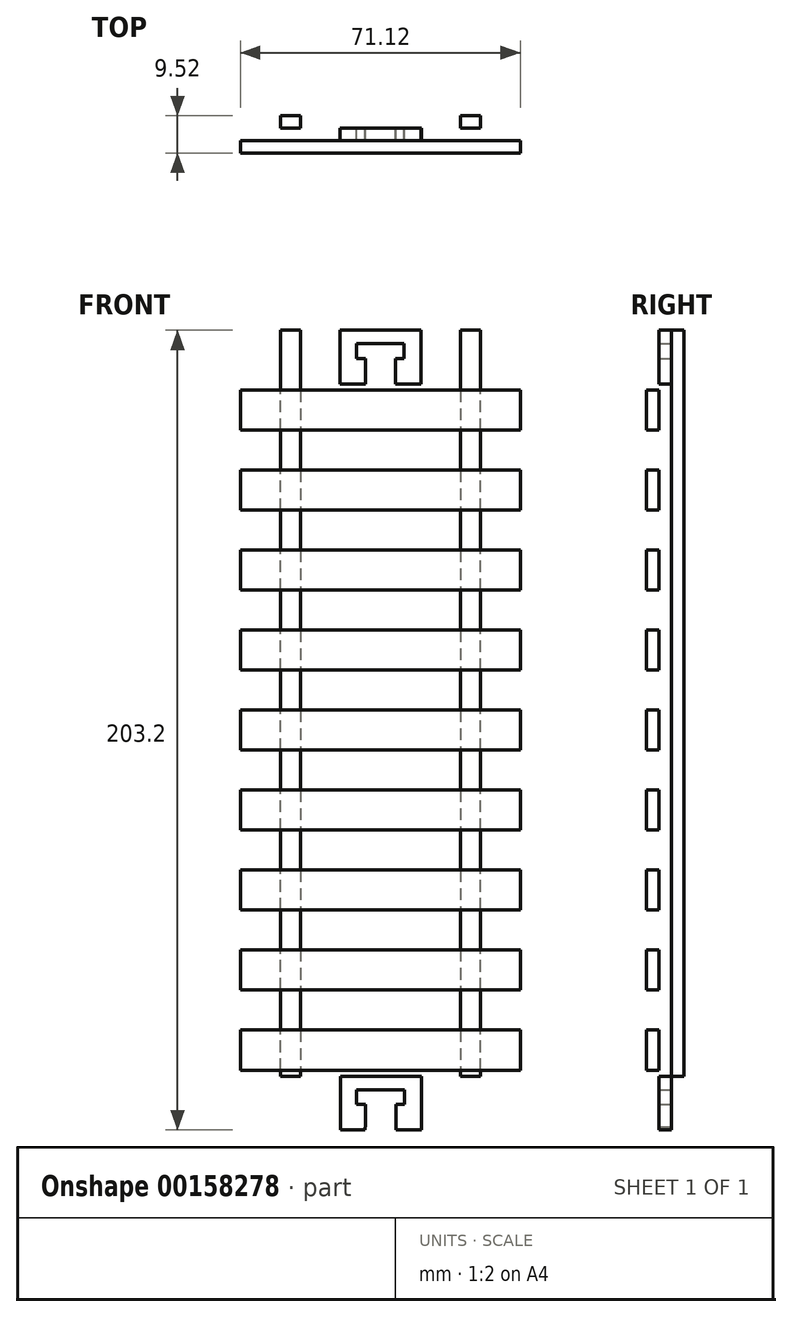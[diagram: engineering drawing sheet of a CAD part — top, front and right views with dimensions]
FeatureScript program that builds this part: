
annotation { "Feature Type Name" : "Feature", "Feature Type Description" : "" }
export const myFeature = defineFeature(function(context is Context, id is Id, definition is map)
    precondition{}
    {
        {
            var Q0;
            Q0=qCreatedBy(makeId("Front.planeOp"),FACE);
            var sketch = newSketch(context, id + "F0", { "sketchPlane" : qUnion([Q0])});
            skLineSegment(sketch, "E0.bottom", {"start": v(0, 72.93) * mm, "end": v(50.8, 72.93) * mm});
            skLineSegment(sketch, "E0.top", {"start": v(0, -130.27) * mm, "end": v(50.8, -130.27) * mm});
            skLineSegment(sketch, "E1", {"start": v(50.8, 72.93) * mm, "end": v(50.8, -130.27) * mm});
            skLineSegment(sketch, "E2", {"start": v(0, 72.93) * mm, "end": v(0, -130.27) * mm});
            skLineSegment(sketch, "E3", {"start": v(0, 72.93) * mm, "end": v(15.11, 72.93) * mm});
            skLineSegment(sketch, "E4", {"start": v(15.11, 72.93) * mm, "end": v(15.11, 59.28) * mm});
            skLineSegment(sketch, "E5", {"start": v(15.11, 59.28) * mm, "end": v(21.6, 59.28) * mm});
            skLineSegment(sketch, "E6", {"start": v(21.6, 59.28) * mm, "end": v(21.6, 65.77) * mm});
            skLineSegment(sketch, "E7", {"start": v(21.6, 65.77) * mm, "end": v(19.38, 65.77) * mm});
            skLineSegment(sketch, "E8", {"start": v(19.38, 65.77) * mm, "end": v(19.38, 69.47) * mm});
            skLineSegment(sketch, "E9", {"start": v(19.38, 69.47) * mm, "end": v(31.43, 69.47) * mm});
            skLineSegment(sketch, "E10", {"start": v(31.43, 69.47) * mm, "end": v(31.43, 65.77) * mm});
            skLineSegment(sketch, "E11", {"start": v(31.43, 65.77) * mm, "end": v(29.22, 65.77) * mm});
            skLineSegment(sketch, "E12", {"start": v(29.22, 65.77) * mm, "end": v(29.22, 59.28) * mm});
            skLineSegment(sketch, "E13", {"start": v(29.22, 59.28) * mm, "end": v(35.7, 59.28) * mm});
            skLineSegment(sketch, "E14", {"start": v(35.7, 59.28) * mm, "end": v(35.7, 72.93) * mm});
            skLineSegment(sketch, "E15", {"start": v(25.4, 72.93) * mm, "end": v(35.7, 72.93) * mm});
            skLineSegment(sketch, "E16", {"start": v(15.11, 72.93) * mm, "end": v(25.4, 72.93) * mm});
            skLineSegment(sketch, "E17", {"start": v(15.1, -130.27) * mm, "end": v(21.58, -130.27) * mm});
            skLineSegment(sketch, "E18", {"start": v(21.58, -130.27) * mm, "end": v(21.58, -123.8) * mm});
            skLineSegment(sketch, "E19", {"start": v(21.58, -123.8) * mm, "end": v(19.37, -123.8) * mm});
            skLineSegment(sketch, "E20", {"start": v(19.37, -123.8) * mm, "end": v(19.37, -120.1) * mm});
            skLineSegment(sketch, "E21", {"start": v(19.37, -120.1) * mm, "end": v(31.58, -120.1) * mm});
            skLineSegment(sketch, "E22", {"start": v(31.58, -120.1) * mm, "end": v(31.58, -123.8) * mm});
            skLineSegment(sketch, "E23", {"start": v(31.58, -123.8) * mm, "end": v(29.37, -123.8) * mm});
            skLineSegment(sketch, "E24", {"start": v(29.37, -123.8) * mm, "end": v(29.37, -130.27) * mm});
            skLineSegment(sketch, "E25", {"start": v(29.37, -130.27) * mm, "end": v(35.84, -130.27) * mm});
            skLineSegment(sketch, "E26", {"start": v(35.84, -130.27) * mm, "end": v(35.84, -116.62) * mm});
            skLineSegment(sketch, "E27", {"start": v(25.55, -116.62) * mm, "end": v(35.84, -116.62) * mm});
            skLineSegment(sketch, "E28", {"start": v(15.26, -116.62) * mm, "end": v(25.55, -116.62) * mm});
            skCircle(sketch, "E29", {"center": v(25.4, -130.27) * mm, "radius": 3.91 * mm});
            skLineSegment(sketch, "E30", {"start": v(15.26, -116.62) * mm, "end": v(15.26, -130.27) * mm});
            skLineSegment(sketch, "E31", {"start": v(15.26, -130.27) * mm, "end": v(35.84, -130.27) * mm});
            skLineSegment(sketch, "E32", {"start": v(15.26, -116.62) * mm, "end": v(0, -116.62) * mm});
            skLineSegment(sketch, "E33", {"start": v(0, -116.62) * mm, "end": v(35.84, -116.62) * mm});
            skLineSegment(sketch, "E34", {"start": v(35.84, -116.62) * mm, "end": v(50.8, -116.62) * mm});
            skSolve(sketch);
        }
        {
            var Q0;
            {var subQ7=sQuery(id+"F0.wireOp",EDGE,"E19");Q0=makeQuery(id+"F0.imprint","IMPRINT",FACE,{"disambiguationData":[TD([[makeQuery(id+"F0.imprint","IMPRINT",EDGE,{"derivedFrom":subQ7}),1.0]])]});}
            var Q1;
            {var subQ0=sQuery(id+"F0.wireOp",EDGE,"E0.bottom");Q1=makeQuery(id+"F0.imprint","IMPRINT",FACE,{"disambiguationData":[TD([[makeQuery(id+"F0.imprint","IMPRINT",EDGE,{"derivedFrom":subQ0}),-1.0]])]});}
            extrude(context, id + "F1", {"entities" : qUnion([Q0, Q1]), "depth" : 3.17 * mm});
        }
        {
            var Q0;
            Q0=makeQuery(id+"F1.opExtrude","CAP_FACE",FACE,{"disambiguationData":[OSD([sQuery(id+"F0.wireOp",EDGE,"E0.bottom"),sQuery(id+"F0.wireOp",EDGE,"E1"),sQuery(id+"F0.wireOp",EDGE,"E2"),sQuery(id+"F0.wireOp",EDGE,"E3"),sQuery(id+"F0.wireOp",EDGE,"E4"),sQuery(id+"F0.wireOp",EDGE,"E5"),sQuery(id+"F0.wireOp",EDGE,"E6"),sQuery(id+"F0.wireOp",EDGE,"E7"),sQuery(id+"F0.wireOp",EDGE,"E8"),sQuery(id+"F0.wireOp",EDGE,"E9"),sQuery(id+"F0.wireOp",EDGE,"E10"),sQuery(id+"F0.wireOp",EDGE,"E11"),sQuery(id+"F0.wireOp",EDGE,"E12"),sQuery(id+"F0.wireOp",EDGE,"E13"),sQuery(id+"F0.wireOp",EDGE,"E14"),sQuery(id+"F0.wireOp",EDGE,"E18"),sQuery(id+"F0.wireOp",EDGE,"E19"),sQuery(id+"F0.wireOp",EDGE,"E20"),sQuery(id+"F0.wireOp",EDGE,"E21"),sQuery(id+"F0.wireOp",EDGE,"E22"),sQuery(id+"F0.wireOp",EDGE,"E23"),sQuery(id+"F0.wireOp",EDGE,"E24"),sQuery(id+"F0.wireOp",EDGE,"E26"),sQuery(id+"F0.wireOp",EDGE,"E29"),sQuery(id+"F0.wireOp",EDGE,"E30"),sQuery(id+"F0.wireOp",EDGE,"E31"),sQuery(id+"F0.wireOp",EDGE,"E33"),sQuery(id+"F0.wireOp",EDGE,"E34")])],"isStart":false});
            var sketch = newSketch(context, id + "F2", { "sketchPlane" : qUnion([Q0])});
            skLineSegment(sketch, "E35", {"start": v(0, 72.93) * mm, "end": v(-10.16, 72.93) * mm});
            skLineSegment(sketch, "E36", {"start": v(-10.16, 72.93) * mm, "end": v(-10.16, -116.62) * mm});
            skLineSegment(sketch, "E37", {"start": v(-10.16, -116.62) * mm, "end": v(0, -116.62) * mm});
            skLineSegment(sketch, "E38", {"start": v(50.8, 72.93) * mm, "end": v(60.96, 72.93) * mm});
            skLineSegment(sketch, "E39", {"start": v(60.96, 72.93) * mm, "end": v(60.96, -116.62) * mm});
            skLineSegment(sketch, "E40", {"start": v(60.96, -116.62) * mm, "end": v(50.8, -116.62) * mm});
            skLineSegment(sketch, "E41", {"start": v(-10.16, 57.66) * mm, "end": v(60.96, 57.66) * mm});
            skLineSegment(sketch, "E42", {"start": v(60.96, 57.66) * mm, "end": v(60.96, 47.5) * mm});
            skLineSegment(sketch, "E43", {"start": v(60.96, 47.5) * mm, "end": v(-10.16, 47.5) * mm});
            skLineSegment(sketch, "E44", {"start": v(-10.16, 47.5) * mm, "end": v(-10.16, 57.66) * mm});
            skLineSegment(sketch, "E45", {"start": v(0, 47.5) * mm, "end": v(0, 37.34) * mm});
            skLineSegment(sketch, "E46", {"start": v(0, 37.34) * mm, "end": v(-10.16, 37.34) * mm});
            skLineSegment(sketch, "E47", {"start": v(-10.16, 37.34) * mm, "end": v(-10.16, 27.18) * mm});
            skLineSegment(sketch, "E48", {"start": v(-10.16, 27.18) * mm, "end": v(60.96, 27.18) * mm});
            skLineSegment(sketch, "E49", {"start": v(60.96, 27.18) * mm, "end": v(60.96, 37.34) * mm});
            skLineSegment(sketch, "E50", {"start": v(60.96, 37.34) * mm, "end": v(0, 37.34) * mm});
            skLineSegment(sketch, "E51", {"start": v(0, 27.18) * mm, "end": v(0, 17.02) * mm});
            skLineSegment(sketch, "E52", {"start": v(0, 17.02) * mm, "end": v(-10.16, 17.02) * mm});
            skLineSegment(sketch, "E53", {"start": v(-10.16, 17.02) * mm, "end": v(-10.16, 6.86) * mm});
            skLineSegment(sketch, "E54", {"start": v(-10.16, 6.86) * mm, "end": v(60.96, 6.86) * mm});
            skLineSegment(sketch, "E55", {"start": v(60.96, 6.86) * mm, "end": v(60.96, 17.02) * mm});
            skLineSegment(sketch, "E56", {"start": v(60.96, 17.02) * mm, "end": v(0, 17.02) * mm});
            skLineSegment(sketch, "E57", {"start": v(0, 6.86) * mm, "end": v(0, -3.3) * mm});
            skLineSegment(sketch, "E58", {"start": v(0, -3.3) * mm, "end": v(-10.16, -3.3) * mm});
            skLineSegment(sketch, "E59", {"start": v(-10.16, -3.3) * mm, "end": v(-10.16, -13.46) * mm});
            skLineSegment(sketch, "E60", {"start": v(-10.16, -13.46) * mm, "end": v(60.96, -13.46) * mm});
            skLineSegment(sketch, "E61", {"start": v(60.96, -13.46) * mm, "end": v(60.96, -3.3) * mm});
            skLineSegment(sketch, "E62", {"start": v(60.96, -3.3) * mm, "end": v(0, -3.3) * mm});
            skLineSegment(sketch, "E63", {"start": v(60.96, -13.46) * mm, "end": v(60.96, -23.62) * mm});
            skLineSegment(sketch, "E64", {"start": v(60.96, -23.62) * mm, "end": v(-10.16, -23.62) * mm});
            skLineSegment(sketch, "E65", {"start": v(-10.16, -23.62) * mm, "end": v(-10.16, -33.78) * mm});
            skLineSegment(sketch, "E66", {"start": v(-10.16, -33.78) * mm, "end": v(60.96, -33.78) * mm});
            skLineSegment(sketch, "E67", {"start": v(60.96, -33.78) * mm, "end": v(60.96, -23.62) * mm});
            skLineSegment(sketch, "E68", {"start": v(-10.16, -33.78) * mm, "end": v(-10.16, -43.94) * mm});
            skLineSegment(sketch, "E69", {"start": v(-10.16, -43.94) * mm, "end": v(60.96, -43.94) * mm});
            skLineSegment(sketch, "E70", {"start": v(60.96, -43.94) * mm, "end": v(60.96, -54.1) * mm});
            skLineSegment(sketch, "E71", {"start": v(60.96, -54.1) * mm, "end": v(-10.16, -54.1) * mm});
            skLineSegment(sketch, "E72", {"start": v(-10.16, -54.1) * mm, "end": v(-10.16, -43.94) * mm});
            skLineSegment(sketch, "E73", {"start": v(-10.16, -54.1) * mm, "end": v(-10.16, -64.26) * mm});
            skLineSegment(sketch, "E74", {"start": v(-10.16, -64.26) * mm, "end": v(60.96, -64.26) * mm});
            skLineSegment(sketch, "E75", {"start": v(60.96, -64.26) * mm, "end": v(60.96, -74.36) * mm});
            skLineSegment(sketch, "E76", {"start": v(60.96, -74.36) * mm, "end": v(-10.16, -74.36) * mm});
            skLineSegment(sketch, "E77", {"start": v(-10.16, -74.36) * mm, "end": v(-10.16, -64.26) * mm});
            skLineSegment(sketch, "E78", {"start": v(60.96, -74.36) * mm, "end": v(60.96, -84.49) * mm});
            skLineSegment(sketch, "E79", {"start": v(60.96, -84.49) * mm, "end": v(-10.16, -84.49) * mm});
            skLineSegment(sketch, "E80", {"start": v(-10.16, -84.49) * mm, "end": v(-10.16, -94.69) * mm});
            skLineSegment(sketch, "E81", {"start": v(-10.16, -94.69) * mm, "end": v(60.96, -94.69) * mm});
            skLineSegment(sketch, "E82", {"start": v(60.96, -94.69) * mm, "end": v(60.96, -104.9) * mm});
            skLineSegment(sketch, "E83", {"start": v(60.96, -104.9) * mm, "end": v(60.96, -115.13) * mm});
            skLineSegment(sketch, "E84", {"start": v(60.96, -115.13) * mm, "end": v(-10.16, -115.13) * mm});
            skLineSegment(sketch, "E85", {"start": v(-10.16, -115.13) * mm, "end": v(-10.16, -104.9) * mm});
            skLineSegment(sketch, "E86", {"start": v(-10.16, -104.9) * mm, "end": v(60.96, -104.9) * mm});
            skSolve(sketch);
        }
        {
            var Q0;
            {var subQ0=sQuery(id+"F2.wireOp",EDGE,"E41");var subQ1=makeQuery(id+"F1.opExtrude","CAP_EDGE",EDGE,{"disambiguationData":[OSD([sQuery(id+"F0.wireOp",EDGE,"E2")])],"isStart":false});var subQ2=makeQuery(id+"F2.imprint","INTERSECT",VERTEX,{"derivedFrom":[subQ1,subQ0]});Q0=makeQuery(id+"F2.imprint","IMPRINT",FACE,{"disambiguationData":[TD([[makeQuery(id+"F2.imprint","IMPRINT",EDGE,{"disambiguationData":[TD([[subQ2,-1.0]])],"derivedFrom":subQ0}),-1.0]])]});}
            var Q1;
            {var subQ0=sQuery(id+"F2.wireOp",EDGE,"E42");Q1=makeQuery(id+"F2.imprint","IMPRINT",FACE,{"disambiguationData":[TD([[makeQuery(id+"F2.imprint","IMPRINT",EDGE,{"derivedFrom":subQ0}),-1.0]])]});}
            var Q2;
            {var subQ0=sQuery(id+"F2.wireOp",EDGE,"E44");Q2=makeQuery(id+"F2.imprint","IMPRINT",FACE,{"disambiguationData":[TD([[makeQuery(id+"F2.imprint","IMPRINT",EDGE,{"derivedFrom":subQ0}),-1.0]])]});}
            var Q3;
            {var subQ0=sQuery(id+"F2.wireOp",EDGE,"E46");Q3=makeQuery(id+"F2.imprint","IMPRINT",FACE,{"disambiguationData":[TD([[makeQuery(id+"F2.imprint","IMPRINT",EDGE,{"derivedFrom":subQ0}),1.0]])]});}
            var Q4;
            {var subQ0=sQuery(id+"F2.wireOp",EDGE,"E48");var subQ3=makeQuery(id+"F1.opExtrude","CAP_EDGE",EDGE,{"disambiguationData":[OSD([sQuery(id+"F0.wireOp",EDGE,"E1")])],"isStart":false});var subQ4=makeQuery(id+"F2.imprint","INTERSECT",VERTEX,{"derivedFrom":[subQ3,subQ0]});Q4=makeQuery(id+"F2.imprint","IMPRINT",FACE,{"disambiguationData":[TD([[makeQuery(id+"F2.imprint","IMPRINT",EDGE,{"disambiguationData":[TD([[subQ4,1.0]])],"derivedFrom":subQ3}),-1.0]])]});}
            var Q5;
            {var subQ0=sQuery(id+"F2.wireOp",EDGE,"E49");Q5=makeQuery(id+"F2.imprint","IMPRINT",FACE,{"disambiguationData":[TD([[makeQuery(id+"F2.imprint","IMPRINT",EDGE,{"derivedFrom":subQ0}),1.0]])]});}
            var Q6;
            {var subQ0=sQuery(id+"F2.wireOp",EDGE,"E55");Q6=makeQuery(id+"F2.imprint","IMPRINT",FACE,{"disambiguationData":[TD([[makeQuery(id+"F2.imprint","IMPRINT",EDGE,{"derivedFrom":subQ0}),1.0]])]});}
            var Q7;
            {var subQ0=sQuery(id+"F2.wireOp",EDGE,"E54");var subQ3=makeQuery(id+"F1.opExtrude","CAP_EDGE",EDGE,{"disambiguationData":[OSD([sQuery(id+"F0.wireOp",EDGE,"E1")])],"isStart":false});var subQ4=makeQuery(id+"F2.imprint","INTERSECT",VERTEX,{"derivedFrom":[subQ3,subQ0]});Q7=makeQuery(id+"F2.imprint","IMPRINT",FACE,{"disambiguationData":[TD([[makeQuery(id+"F2.imprint","IMPRINT",EDGE,{"disambiguationData":[TD([[subQ4,1.0]])],"derivedFrom":subQ3}),-1.0]])]});}
            var Q8;
            {var subQ0=sQuery(id+"F2.wireOp",EDGE,"E52");Q8=makeQuery(id+"F2.imprint","IMPRINT",FACE,{"disambiguationData":[TD([[makeQuery(id+"F2.imprint","IMPRINT",EDGE,{"derivedFrom":subQ0}),1.0]])]});}
            var Q9;
            {var subQ0=sQuery(id+"F2.wireOp",EDGE,"E58");Q9=makeQuery(id+"F2.imprint","IMPRINT",FACE,{"disambiguationData":[TD([[makeQuery(id+"F2.imprint","IMPRINT",EDGE,{"derivedFrom":subQ0}),1.0]])]});}
            var Q10;
            {var subQ0=sQuery(id+"F2.wireOp",EDGE,"E60");var subQ1=makeQuery(id+"F1.opExtrude","CAP_EDGE",EDGE,{"disambiguationData":[OSD([sQuery(id+"F0.wireOp",EDGE,"E2")])],"isStart":false});var subQ2=makeQuery(id+"F2.imprint","INTERSECT",VERTEX,{"derivedFrom":[subQ1,subQ0]});Q10=makeQuery(id+"F2.imprint","IMPRINT",FACE,{"disambiguationData":[TD([[makeQuery(id+"F2.imprint","IMPRINT",EDGE,{"disambiguationData":[TD([[subQ2,-1.0]])],"derivedFrom":subQ0}),1.0]])]});}
            var Q11;
            {var subQ0=sQuery(id+"F2.wireOp",EDGE,"E61");Q11=makeQuery(id+"F2.imprint","IMPRINT",FACE,{"disambiguationData":[TD([[makeQuery(id+"F2.imprint","IMPRINT",EDGE,{"derivedFrom":subQ0}),1.0]])]});}
            var Q12;
            {var subQ0=sQuery(id+"F2.wireOp",EDGE,"E67");Q12=makeQuery(id+"F2.imprint","IMPRINT",FACE,{"disambiguationData":[TD([[makeQuery(id+"F2.imprint","IMPRINT",EDGE,{"derivedFrom":subQ0}),1.0]])]});}
            var Q13;
            {var subQ0=sQuery(id+"F2.wireOp",EDGE,"E64");var subQ1=makeQuery(id+"F1.opExtrude","CAP_EDGE",EDGE,{"disambiguationData":[OSD([sQuery(id+"F0.wireOp",EDGE,"E1")])],"isStart":false});var subQ2=makeQuery(id+"F2.imprint","INTERSECT",VERTEX,{"derivedFrom":[subQ1,subQ0]});Q13=makeQuery(id+"F2.imprint","IMPRINT",FACE,{"disambiguationData":[TD([[makeQuery(id+"F2.imprint","IMPRINT",EDGE,{"disambiguationData":[TD([[subQ2,-1.0]])],"derivedFrom":subQ0}),1.0]])]});}
            var Q14;
            {var subQ0=sQuery(id+"F2.wireOp",EDGE,"E65");Q14=makeQuery(id+"F2.imprint","IMPRINT",FACE,{"disambiguationData":[TD([[makeQuery(id+"F2.imprint","IMPRINT",EDGE,{"derivedFrom":subQ0}),1.0]])]});}
            var Q15;
            {var subQ0=sQuery(id+"F2.wireOp",EDGE,"E72");Q15=makeQuery(id+"F2.imprint","IMPRINT",FACE,{"disambiguationData":[TD([[makeQuery(id+"F2.imprint","IMPRINT",EDGE,{"derivedFrom":subQ0}),-1.0]])]});}
            var Q16;
            {var subQ0=sQuery(id+"F2.wireOp",EDGE,"E69");var subQ1=makeQuery(id+"F1.opExtrude","CAP_EDGE",EDGE,{"disambiguationData":[OSD([sQuery(id+"F0.wireOp",EDGE,"E2")])],"isStart":false});var subQ2=makeQuery(id+"F2.imprint","INTERSECT",VERTEX,{"derivedFrom":[subQ1,subQ0]});Q16=makeQuery(id+"F2.imprint","IMPRINT",FACE,{"disambiguationData":[TD([[makeQuery(id+"F2.imprint","IMPRINT",EDGE,{"disambiguationData":[TD([[subQ2,-1.0]])],"derivedFrom":subQ0}),-1.0]])]});}
            var Q17;
            {var subQ0=sQuery(id+"F2.wireOp",EDGE,"E70");Q17=makeQuery(id+"F2.imprint","IMPRINT",FACE,{"disambiguationData":[TD([[makeQuery(id+"F2.imprint","IMPRINT",EDGE,{"derivedFrom":subQ0}),-1.0]])]});}
            var Q18;
            {var subQ0=sQuery(id+"F2.wireOp",EDGE,"E75");Q18=makeQuery(id+"F2.imprint","IMPRINT",FACE,{"disambiguationData":[TD([[makeQuery(id+"F2.imprint","IMPRINT",EDGE,{"derivedFrom":subQ0}),-1.0]])]});}
            var Q19;
            {var subQ0=sQuery(id+"F2.wireOp",EDGE,"E74");var subQ1=makeQuery(id+"F1.opExtrude","CAP_EDGE",EDGE,{"disambiguationData":[OSD([sQuery(id+"F0.wireOp",EDGE,"E2")])],"isStart":false});var subQ2=makeQuery(id+"F2.imprint","INTERSECT",VERTEX,{"derivedFrom":[subQ1,subQ0]});Q19=makeQuery(id+"F2.imprint","IMPRINT",FACE,{"disambiguationData":[TD([[makeQuery(id+"F2.imprint","IMPRINT",EDGE,{"disambiguationData":[TD([[subQ2,-1.0]])],"derivedFrom":subQ0}),-1.0]])]});}
            var Q20;
            {var subQ0=sQuery(id+"F2.wireOp",EDGE,"E77");Q20=makeQuery(id+"F2.imprint","IMPRINT",FACE,{"disambiguationData":[TD([[makeQuery(id+"F2.imprint","IMPRINT",EDGE,{"derivedFrom":subQ0}),-1.0]])]});}
            var Q21;
            {var subQ0=sQuery(id+"F2.wireOp",EDGE,"E80");Q21=makeQuery(id+"F2.imprint","IMPRINT",FACE,{"disambiguationData":[TD([[makeQuery(id+"F2.imprint","IMPRINT",EDGE,{"derivedFrom":subQ0}),1.0]])]});}
            var Q22;
            {var subQ0=sQuery(id+"F2.wireOp",EDGE,"E79");var subQ1=makeQuery(id+"F1.opExtrude","CAP_EDGE",EDGE,{"disambiguationData":[OSD([sQuery(id+"F0.wireOp",EDGE,"E1")])],"isStart":false});var subQ2=makeQuery(id+"F2.imprint","INTERSECT",VERTEX,{"derivedFrom":[subQ1,subQ0]});Q22=makeQuery(id+"F2.imprint","IMPRINT",FACE,{"disambiguationData":[TD([[makeQuery(id+"F2.imprint","IMPRINT",EDGE,{"disambiguationData":[TD([[subQ2,-1.0]])],"derivedFrom":subQ0}),1.0]])]});}
            var Q23;
            {var subQ0=sQuery(id+"F2.wireOp",EDGE,"E79");var subQ5=makeQuery(id+"F1.opExtrude","CAP_EDGE",EDGE,{"disambiguationData":[OSD([sQuery(id+"F0.wireOp",EDGE,"E1")])],"isStart":false});var subQ6=makeQuery(id+"F2.imprint","INTERSECT",VERTEX,{"derivedFrom":[subQ5,subQ0]});Q23=makeQuery(id+"F2.imprint","IMPRINT",FACE,{"disambiguationData":[TD([[makeQuery(id+"F2.imprint","IMPRINT",EDGE,{"disambiguationData":[TD([[subQ6,-1.0]])],"derivedFrom":subQ5}),1.0]])]});}
            extrude(context, id + "F3", {"entities" : qUnion([Q0, Q1, Q2, Q3, Q4, Q5, Q6, Q7, Q8, Q9, Q10, Q11, Q12, Q13, Q14, Q15, Q16, Q17, Q18, Q19, Q20, Q21, Q22, Q23]), "operationType" : NewBodyOperationType.ADD, "depth" : 3.17 * mm});
        }
        {
            var Q0;
            {var subQ0=sQuery(id+"F2.wireOp",EDGE,"E84");var subQ1=makeQuery(id+"F1.opExtrude","CAP_EDGE",EDGE,{"disambiguationData":[OSD([sQuery(id+"F0.wireOp",EDGE,"E1")])],"isStart":false});var subQ2=makeQuery(id+"F2.imprint","INTERSECT",VERTEX,{"derivedFrom":[subQ1,subQ0]});Q0=makeQuery(id+"F2.imprint","IMPRINT",FACE,{"disambiguationData":[TD([[makeQuery(id+"F2.imprint","IMPRINT",EDGE,{"disambiguationData":[TD([[subQ2,-1.0]])],"derivedFrom":subQ0}),-1.0]])]});}
            var Q1;
            {var subQ0=sQuery(id+"F2.wireOp",EDGE,"E83");Q1=makeQuery(id+"F2.imprint","IMPRINT",FACE,{"disambiguationData":[TD([[makeQuery(id+"F2.imprint","IMPRINT",EDGE,{"derivedFrom":subQ0}),-1.0]])]});}
            var Q2;
            {var subQ0=sQuery(id+"F2.wireOp",EDGE,"E85");Q2=makeQuery(id+"F2.imprint","IMPRINT",FACE,{"disambiguationData":[TD([[makeQuery(id+"F2.imprint","IMPRINT",EDGE,{"derivedFrom":subQ0}),-1.0]])]});}
            extrude(context, id + "F4", {"entities" : qUnion([Q0, Q1, Q2]), "operationType" : NewBodyOperationType.ADD, "depth" : 3.17 * mm});
        }
        {
            var Q0;
            Q0=makeQuery(id+"F1.opExtrude","CAP_FACE",FACE,{"disambiguationData":[OSD([sQuery(id+"F0.wireOp",EDGE,"E0.bottom"),sQuery(id+"F0.wireOp",EDGE,"E1"),sQuery(id+"F0.wireOp",EDGE,"E2"),sQuery(id+"F0.wireOp",EDGE,"E3"),sQuery(id+"F0.wireOp",EDGE,"E4"),sQuery(id+"F0.wireOp",EDGE,"E5"),sQuery(id+"F0.wireOp",EDGE,"E6"),sQuery(id+"F0.wireOp",EDGE,"E7"),sQuery(id+"F0.wireOp",EDGE,"E8"),sQuery(id+"F0.wireOp",EDGE,"E9"),sQuery(id+"F0.wireOp",EDGE,"E10"),sQuery(id+"F0.wireOp",EDGE,"E11"),sQuery(id+"F0.wireOp",EDGE,"E12"),sQuery(id+"F0.wireOp",EDGE,"E13"),sQuery(id+"F0.wireOp",EDGE,"E14"),sQuery(id+"F0.wireOp",EDGE,"E18"),sQuery(id+"F0.wireOp",EDGE,"E19"),sQuery(id+"F0.wireOp",EDGE,"E20"),sQuery(id+"F0.wireOp",EDGE,"E21"),sQuery(id+"F0.wireOp",EDGE,"E22"),sQuery(id+"F0.wireOp",EDGE,"E23"),sQuery(id+"F0.wireOp",EDGE,"E24"),sQuery(id+"F0.wireOp",EDGE,"E26"),sQuery(id+"F0.wireOp",EDGE,"E29"),sQuery(id+"F0.wireOp",EDGE,"E30"),sQuery(id+"F0.wireOp",EDGE,"E31"),sQuery(id+"F0.wireOp",EDGE,"E33"),sQuery(id+"F0.wireOp",EDGE,"E34")])],"isStart":true});
            var sketch = newSketch(context, id + "F5", { "sketchPlane" : qUnion([Q0])});
            skLineSegment(sketch, "E87", {"start": v(-50.8, 72.93) * mm, "end": v(-45.7, 72.93) * mm});
            skLineSegment(sketch, "E88", {"start": v(-45.7, 72.93) * mm, "end": v(-45.7, -116.62) * mm});
            skLineSegment(sketch, "E89", {"start": v(-45.7, -116.62) * mm, "end": v(-50.8, -116.62) * mm});
            skLineSegment(sketch, "E90", {"start": v(-50.8, -116.62) * mm, "end": v(-50.8, 72.93) * mm});
            skLineSegment(sketch, "E91", {"start": v(0, 72.93) * mm, "end": v(-5.05, 72.93) * mm});
            skLineSegment(sketch, "E92", {"start": v(-5.05, 72.93) * mm, "end": v(-5.05, -116.62) * mm});
            skPoint(sketch, "E92.endSnap0", {"position": v(-7.63, -116.62) * mm});
            skLineSegment(sketch, "E93", {"start": v(-5.05, -116.62) * mm, "end": v(0, -116.62) * mm});
            skLineSegment(sketch, "E94", {"start": v(0, -116.62) * mm, "end": v(0, 72.93) * mm});
            skSolve(sketch);
        }
        {
            var Q0;
            Q0=qSketchRegion(id+"F5",true);
            extrude(context, id + "F6", {"entities" : qUnion([Q0]), "operationType" : NewBodyOperationType.ADD, "depth" : 3.17 * mm});
        }
    });
